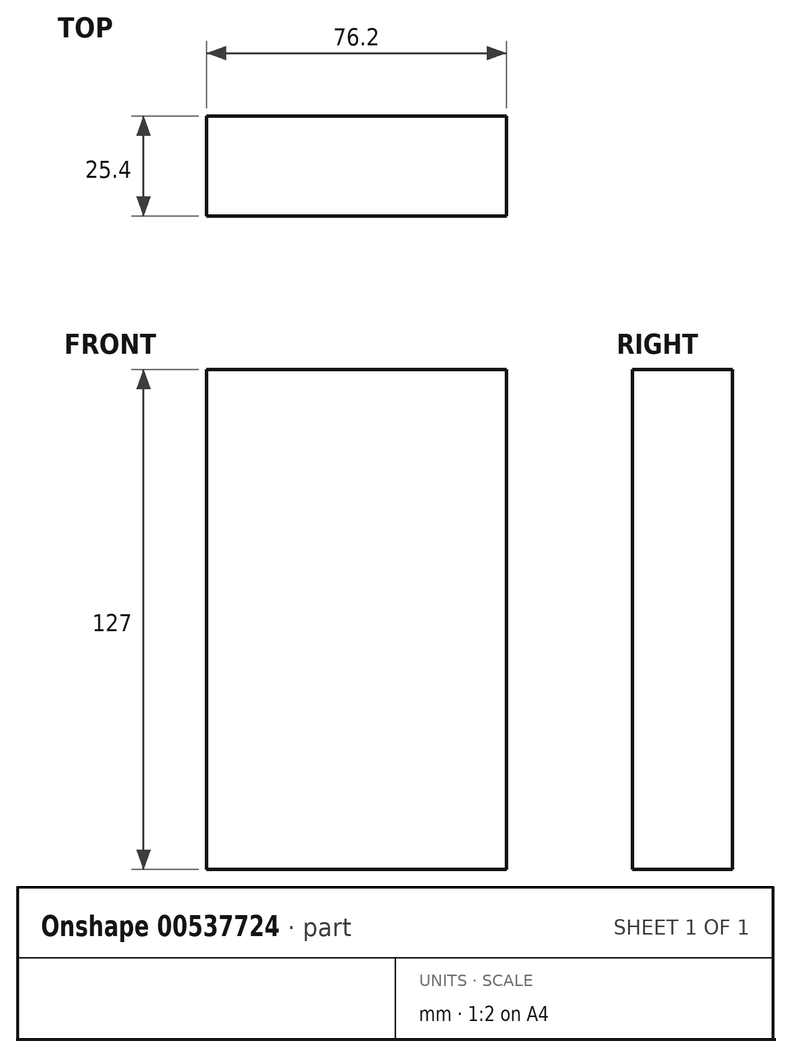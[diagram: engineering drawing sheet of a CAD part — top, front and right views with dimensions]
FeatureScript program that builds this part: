
annotation { "Feature Type Name" : "Feature", "Feature Type Description" : "" }
export const myFeature = defineFeature(function(context is Context, id is Id, definition is map)
    precondition{}
    {
        {
            var Q0;
            Q0=qCreatedBy(makeId("Front.planeOp"),FACE);
            var sketch = newSketch(context, id + "F0", { "sketchPlane" : qUnion([Q0])});
            skLineSegment(sketch, "E0", {"start": v(24.17, 57.2) * mm, "end": v(-52.03, 57.2) * mm});
            skLineSegment(sketch, "E1", {"start": v(-52.03, 57.2) * mm, "end": v(-52.03, -69.8) * mm});
            skLineSegment(sketch, "E2", {"start": v(-52.03, -69.8) * mm, "end": v(24.17, -69.8) * mm});
            skLineSegment(sketch, "E3", {"start": v(24.17, -69.8) * mm, "end": v(24.17, 57.2) * mm});
            skSolve(sketch);
        }
        {
            var Q0;
            Q0 = qSketchRegion(id + "F0", true);
            extrude(context, id + "F1", {"entities" : qUnion([Q0]), "depth" : 25.4 * mm, "offsetDistance" : 25.4 * mm});
        }
    });
